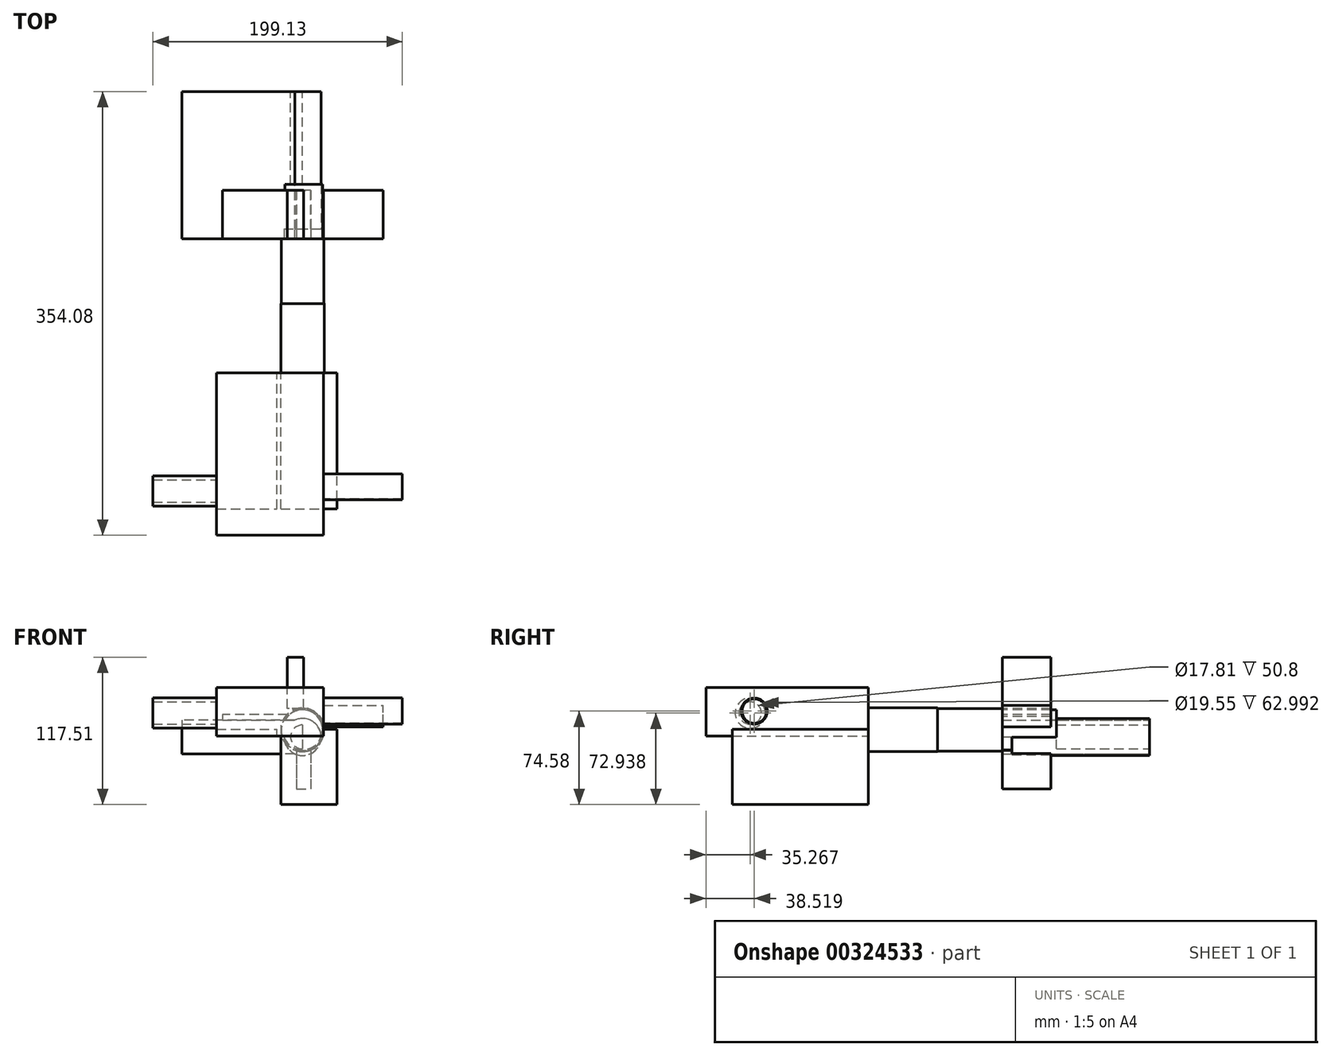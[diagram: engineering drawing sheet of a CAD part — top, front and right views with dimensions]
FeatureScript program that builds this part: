
annotation { "Feature Type Name" : "Feature", "Feature Type Description" : "" }
export const myFeature = defineFeature(function(context is Context, id is Id, definition is map)
    precondition{}
    {
        {
            var Q0;
            Q0=qCreatedBy(makeId("Front.planeOp"),FACE);
            var sketch = newSketch(context, id + "F0", { "sketchPlane" : qUnion([Q0])});
            skLineSegment(sketch, "E0.bottom", {"start": v(108.4, 61.05) * mm, "end": v(11.92, 61.05) * mm});
            skLineSegment(sketch, "E0.top", {"start": v(108.4, 34.26) * mm, "end": v(11.92, 34.26) * mm});
            skLineSegment(sketch, "E0.left", {"start": v(108.4, 61.05) * mm, "end": v(108.4, 34.26) * mm});
            skLineSegment(sketch, "E0.right", {"start": v(11.92, 61.05) * mm, "end": v(11.92, 34.26) * mm});
            skCircle(sketch, "E1", {"center": v(108.4, 47.66) * mm, "radius": 9.54 * mm});
            skCircle(sketch, "E2", {"center": v(108.4, 47.66) * mm, "radius": 14.8 * mm});
            skSolve(sketch);
        }
        {
            var Q0;
            {var subQ4=sQuery(id+"F0.wireOp",EDGE,"E0.bottom");Q0=makeQuery(id+"F0.imprint","IMPRINT",FACE,{"disambiguationData":[TD([[makeQuery(id+"F0.imprint","IMPRINT",EDGE,{"derivedFrom":subQ4}),1.0]])]});}
            var Q1;
            {var subQ0=sQuery(id+"F0.wireOp",EDGE,"E1");var subQ1=sQuery(id+"F0.wireOp",EDGE,"E0.left");var subQ2=makeQuery(id+"F0.imprint","INTERSECT",VERTEX,{"disambiguationData":[OD(0.0)],"derivedFrom":[subQ1,subQ0]});Q1=makeQuery(id+"F0.imprint","IMPRINT",FACE,{"disambiguationData":[TD([[makeQuery(id+"F0.imprint","IMPRINT",EDGE,{"disambiguationData":[TD([[subQ2,-1.0]])],"derivedFrom":subQ1}),1.0]])]});}
            extrude(context, id + "F1", {"entities" : qUnion([Q0, Q1]), "depth" : 117.6 * mm});
        }
        {
            var Q0;
            Q0 = qSketchRegion(id + "F0", true);
            extrude(context, id + "F2", {"entities" : qUnion([Q0]), "depth" : 109.73 * mm});
        }
        {
            var Q0;
            Q0=makeQuery(id+"F1.opExtrude","CAP_FACE",FACE,{"disambiguationData":[OSD([sQuery(id+"F0.wireOp",EDGE,"E0.left"),sQuery(id+"F0.wireOp",EDGE,"E1")])],"isStart":false});
            var sketch = newSketch(context, id + "F3", { "sketchPlane" : qUnion([Q0])});
            skCircle(sketch, "E3", {"center": v(108.4, 53.4) * mm, "radius": 17 * mm});
            skSolve(sketch);
        }
        {
            var Q0;
            Q0 = qSketchRegion(id + "F3", true);
            extrude(context, id + "F4", {"entities" : qUnion([Q0]), "depth" : 51.56 * mm});
        }
        {
            var Q0;
            Q0=makeQuery(id+"F4.opExtrude","CAP_FACE",FACE,{"disambiguationData":[OSD([sQuery(id+"F3.wireOp",EDGE,"E3")])],"isStart":true});
            var sketch = newSketch(context, id + "F5", { "sketchPlane" : qUnion([Q0])});
            skLineSegment(sketch, "E4.bottom", {"start": v(-125.23, 55.7) * mm, "end": v(-172.85, 55.7) * mm});
            skLineSegment(sketch, "E4.top", {"start": v(-125.23, 72.72) * mm, "end": v(-172.85, 72.72) * mm});
            skLineSegment(sketch, "E4.left", {"start": v(-125.23, 55.7) * mm, "end": v(-125.23, 72.72) * mm});
            skLineSegment(sketch, "E4.right", {"start": v(-172.85, 55.7) * mm, "end": v(-172.85, 72.72) * mm});
            skLineSegment(sketch, "E5.bottom", {"start": v(-96.5, 65.53) * mm, "end": v(-44.31, 65.53) * mm});
            skLineSegment(sketch, "E5.top", {"start": v(-96.5, 51.24) * mm, "end": v(-44.31, 51.24) * mm});
            skLineSegment(sketch, "E5.left", {"start": v(-96.5, 65.53) * mm, "end": v(-96.5, 51.24) * mm});
            skLineSegment(sketch, "E5.right", {"start": v(-44.31, 65.53) * mm, "end": v(-44.31, 51.24) * mm});
            skLineSegment(sketch, "E6.bottom", {"start": v(-103.55, 37.12) * mm, "end": v(-114.97, 37.12) * mm});
            skLineSegment(sketch, "E6.top", {"start": v(-103.55, 6.35) * mm, "end": v(-114.97, 6.35) * mm});
            skLineSegment(sketch, "E6.left", {"start": v(-103.55, 37.12) * mm, "end": v(-103.55, 6.35) * mm});
            skLineSegment(sketch, "E6.right", {"start": v(-114.97, 37.12) * mm, "end": v(-114.97, 6.35) * mm});
            skPoint(sketch, "E7.firstSnap0", {"position": v(-109.26, 37.12) * mm});
            skLineSegment(sketch, "E7.bottom", {"start": v(-109.26, 70.37) * mm, "end": v(-96.17, 70.37) * mm});
            skLineSegment(sketch, "E7.top", {"start": v(-109.26, 111.28) * mm, "end": v(-96.17, 111.28) * mm});
            skLineSegment(sketch, "E7.left", {"start": v(-109.26, 70.37) * mm, "end": v(-109.26, 111.28) * mm});
            skLineSegment(sketch, "E7.right", {"start": v(-96.17, 70.37) * mm, "end": v(-96.17, 111.28) * mm});
            skSolve(sketch);
        }
        {
            var Q0;
            Q0 = qSketchRegion(id + "F5", true);
            extrude(context, id + "F6", {"entities" : qUnion([Q0]), "operationType" : NewBodyOperationType.ADD, "depth" : 38.86 * mm});
        }
        {
            var Q0;
            Q0=makeQuery(id+"F4.opExtrude","CAP_FACE",FACE,{"disambiguationData":[OSD([sQuery(id+"F3.wireOp",EDGE,"E3")])],"isStart":true});
            var sketch = newSketch(context, id + "F7", { "sketchPlane" : qUnion([Q0])});
            skCircle(sketch, "E8", {"center": v(-108.4, 53.4) * mm, "radius": 15.94 * mm});
            skSolve(sketch);
        }
        {
            var Q0;
            Q0 = qSketchRegion(id + "F7", true);
            extrude(context, id + "F8", {"entities" : qUnion([Q0]), "operationType" : NewBodyOperationType.ADD, "depth" : 43.43 * mm});
        }
        {
            var Q0;
            Q0=makeQuery(id+"F4.opExtrude","CAP_FACE",FACE,{"disambiguationData":[OSD([sQuery(id+"F3.wireOp",EDGE,"E3")])],"isStart":false});
            var sketch = newSketch(context, id + "F9", { "sketchPlane" : qUnion([Q0])});
            skCircle(sketch, "E9", {"center": v(108.4, 53.4) * mm, "radius": 17.44 * mm});
            skSolve(sketch);
        }
        {
            var Q0;
            Q0 = qSketchRegion(id + "F9", true);
            extrude(context, id + "F10", {"entities" : qUnion([Q0]), "operationType" : NewBodyOperationType.ADD, "depth" : 55.37 * mm});
        }
        {
            var Q0;
            Q0=makeQuery(id+"F10.opExtrude","CAP_FACE",FACE,{"disambiguationData":[OSD([sQuery(id+"F9.wireOp",EDGE,"E9")])],"isStart":false});
            var sketch = newSketch(context, id + "F11", { "sketchPlane" : qUnion([Q0])});
            skLineSegment(sketch, "E10.bottom", {"start": v(90.96, 53.96) * mm, "end": v(135.77, 53.96) * mm});
            skLineSegment(sketch, "E10.top", {"start": v(90.96, -6.23) * mm, "end": v(135.77, -6.23) * mm});
            skLineSegment(sketch, "E10.left", {"start": v(90.96, 53.96) * mm, "end": v(90.96, -6.23) * mm});
            skLineSegment(sketch, "E10.right", {"start": v(135.77, 53.96) * mm, "end": v(135.77, -6.23) * mm});
            skSolve(sketch);
        }
        {
            var Q0;
            Q0 = qSketchRegion(id + "F11", true);
            extrude(context, id + "F12", {"entities" : qUnion([Q0]), "operationType" : NewBodyOperationType.ADD, "depth" : 108.46 * mm});
        }
        {
            var Q0;
            Q0=makeQuery(id+"F10.opExtrude","CAP_FACE",FACE,{"disambiguationData":[OSD([sQuery(id+"F9.wireOp",EDGE,"E9")])],"isStart":false});
            var sketch = newSketch(context, id + "F13", { "sketchPlane" : qUnion([Q0])});
            skLineSegment(sketch, "E11.bottom", {"start": v(125.08, 48.36) * mm, "end": v(88, 48.36) * mm});
            skLineSegment(sketch, "E11.top", {"start": v(125.08, 61.66) * mm, "end": v(88, 61.66) * mm});
            skLineSegment(sketch, "E11.left", {"start": v(125.08, 48.36) * mm, "end": v(125.08, 61.66) * mm});
            skLineSegment(sketch, "E11.right", {"start": v(88, 48.36) * mm, "end": v(88, 61.66) * mm});
            skSolve(sketch);
        }
        {
            var Q0;
            Q0 = qSketchRegion(id + "F13", true);
            extrude(context, id + "F14", {"entities" : qUnion([Q0]), "operationType" : NewBodyOperationType.ADD, "depth" : 129.54 * mm});
        }
        {
            var Q0;
            Q0=makeQuery(id+"F14.opExtrude","SWEPT_FACE",FACE,{"disambiguationData":[OSD([sQuery(id+"F13.wireOp",EDGE,"E11.top")])]});
            extrude(context, id + "F15", {"entities" : qUnion([Q0]), "operationType" : NewBodyOperationType.ADD, "depth" : 25.4 * mm});
        }
        {
            var Q0;
            {var subQ0=sQuery(id+"F13.wireOp",EDGE,"E11.left");Q0=makeQuery(id+"F15.boolean.opBoolean","MERGE",FACE,{"derivedFrom":[makeQuery(id+"F14.opExtrude","SWEPT_FACE",FACE,{"disambiguationData":[OSD([subQ0])]}),makeQuery(id+"F15.opExtrude","SWEPT_FACE",FACE,{"disambiguationData":[OSD([sQuery(id+"F13.wireOp",EDGE,"E11.top"),subQ0])]})]});}
            var sketch = newSketch(context, id + "F16", { "sketchPlane" : qUnion([Q0])});
            skCircle(sketch, "E12", {"center": v(-322.83, 69.73) * mm, "radius": 8.67 * mm});
            skCircle(sketch, "E13", {"center": v(-322.83, 69.73) * mm, "radius": 9.02 * mm});
            skSolve(sketch);
        }
        {
            var Q0;
            Q0 = qSketchRegion(id + "F16", true);
            var Q1;
            Q1=makeQuery(id+"F16.imprint","IMPRINT",FACE,{"disambiguationData":[TD([[makeQuery(id+"F16.imprint","IMPRINT",EDGE,{"derivedFrom":sQuery(id+"F16.wireOp",EDGE,"E12")}),1.0]])]});
            var Q2;
            Q2=makeQuery(id+"F16.imprint","IMPRINT",FACE,{"disambiguationData":[TD([[makeQuery(id+"F16.imprint","IMPRINT",EDGE,{"derivedFrom":sQuery(id+"F16.wireOp",EDGE,"E13")}),-1.0]])]});
            extrude(context, id + "F17", {"entities" : qUnion([Q0, Q1, Q2]), "operationType" : NewBodyOperationType.ADD, "oppositeDirection" : true, "depth" : 85.34 * mm});
        }
        {
            var Q0;
            {var subQ0=sQuery(id+"F13.wireOp",EDGE,"E11.left");Q0=makeQuery(id+"F15.boolean.opBoolean","MERGE",FACE,{"derivedFrom":[makeQuery(id+"F14.opExtrude","SWEPT_FACE",FACE,{"disambiguationData":[OSD([subQ0])]}),makeQuery(id+"F15.opExtrude","SWEPT_FACE",FACE,{"disambiguationData":[OSD([sQuery(id+"F13.wireOp",EDGE,"E11.top"),subQ0])]})]});}
            var sketch = newSketch(context, id + "F18", { "sketchPlane" : qUnion([Q0])});
            skCircle(sketch, "E14", {"center": v(-318.81, 66.7) * mm, "radius": 8.9 * mm});
            skCircle(sketch, "E15", {"center": v(-318.81, 66.7) * mm, "radius": 12.06 * mm});
            skSolve(sketch);
        }
        {
            var Q0;
            Q0 = qSketchRegion(id + "F18", true);
            extrude(context, id + "F19", {"entities" : qUnion([Q0]), "operationType" : NewBodyOperationType.ADD, "oppositeDirection" : true, "depth" : 136.14 * mm});
        }
        {
            var Q0;
            {var subQ0=sQuery(id+"F13.wireOp",EDGE,"E11.left");Q0=makeQuery(id+"F15.boolean.opBoolean","MERGE",FACE,{"derivedFrom":[makeQuery(id+"F14.opExtrude","SWEPT_FACE",FACE,{"disambiguationData":[OSD([subQ0])]}),makeQuery(id+"F15.opExtrude","SWEPT_FACE",FACE,{"disambiguationData":[OSD([sQuery(id+"F13.wireOp",EDGE,"E11.top"),subQ0])]})]});}
            var sketch = newSketch(context, id + "F20", { "sketchPlane" : qUnion([Q0])});
            skCircle(sketch, "E16", {"center": v(-315.56, 68.35) * mm, "radius": 9.77 * mm});
            skCircle(sketch, "E17", {"center": v(-315.56, 68.35) * mm, "radius": 10.41 * mm});
            skSolve(sketch);
        }
        {
            var Q0;
            Q0 = qSketchRegion(id + "F20", true);
            extrude(context, id + "F21", {"entities" : qUnion([Q0]), "operationType" : NewBodyOperationType.ADD, "depth" : 63 * mm});
        }
    });
